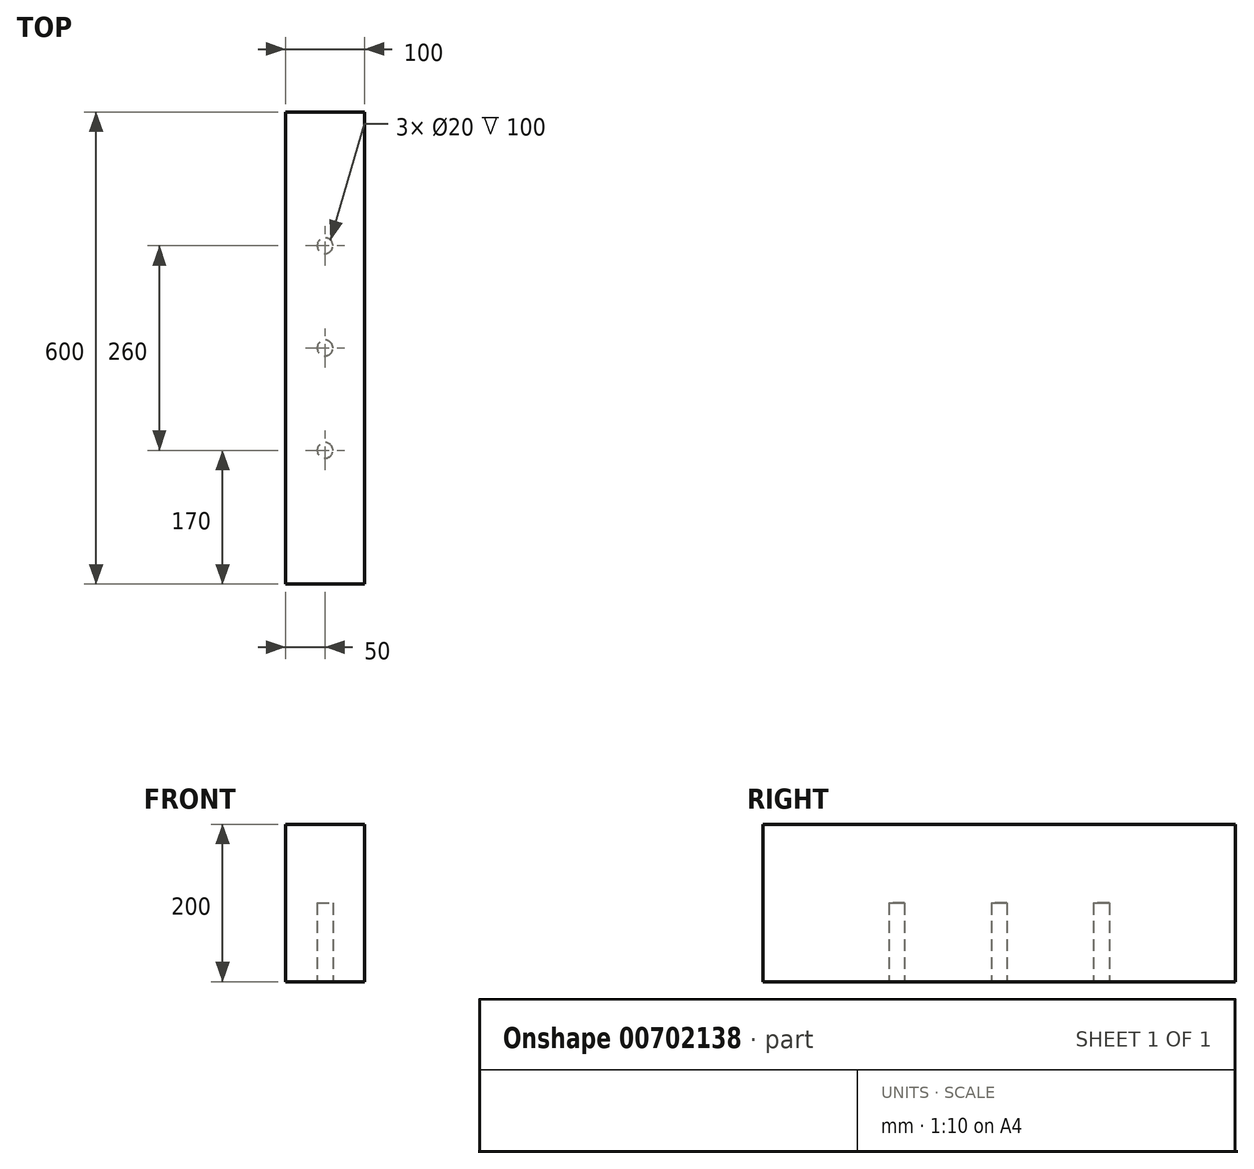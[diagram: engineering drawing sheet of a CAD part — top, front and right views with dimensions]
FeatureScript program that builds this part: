
annotation { "Feature Type Name" : "Feature", "Feature Type Description" : "" }
export const myFeature = defineFeature(function(context is Context, id is Id, definition is map)
    precondition{}
    {
        {
            var Q0;
            Q0=qCreatedBy(makeId("Front.planeOp"),FACE);
            var sketch = newSketch(context, id + "F0", { "sketchPlane" : qUnion([Q0])});
            skLineSegment(sketch, "E0.bottom", {"start": v(0, 0) * mm, "end": v(-100, 0) * mm});
            skLineSegment(sketch, "E0.top", {"start": v(0, 200) * mm, "end": v(-100, 200) * mm});
            skLineSegment(sketch, "E0.left", {"start": v(0, 0) * mm, "end": v(0, 200) * mm});
            skLineSegment(sketch, "E0.right", {"start": v(-100, 0) * mm, "end": v(-100, 200) * mm});
            skSolve(sketch);
        }
        {
            var Q0;
            Q0=qSketchRegion(id+"F0",true);
            extrude(context, id + "F1", {"entities" : qUnion([Q0]), "depth" : 600 * mm, "offsetDistance" : 25 * mm});
        }
        {
            var Q0;
            Q0=makeQuery(id+"F1.opExtrude","SWEPT_FACE",FACE,{"disambiguationData":[OSD([sQuery(id+"F0.wireOp",EDGE,"E0.bottom")])]});
            var sketch = newSketch(context, id + "F2", { "sketchPlane" : qUnion([Q0])});
            skCircle(sketch, "E1", {"center": v(-50, 430) * mm, "radius": 10 * mm});
            skPoint(sketch, "E1.centerSnap0", {"position": v(-50, 600) * mm});
            skCircle(sketch, "E2", {"center": v(-50, 170) * mm, "radius": 10 * mm});
            skPoint(sketch, "E2.centerSnap0", {"position": v(-50, 0) * mm});
            skCircle(sketch, "E3", {"center": v(-50, 300) * mm, "radius": 10 * mm});
            skSolve(sketch);
        }
        {
            var Q0;
            Q0 = qSketchRegion(id + "F2", true);
            extrude(context, id + "F3", {"entities" : qUnion([Q0]), "operationType" : NewBodyOperationType.REMOVE, "oppositeDirection" : true, "depth" : 100 * mm, "offsetDistance" : 25 * mm});
        }
    });
